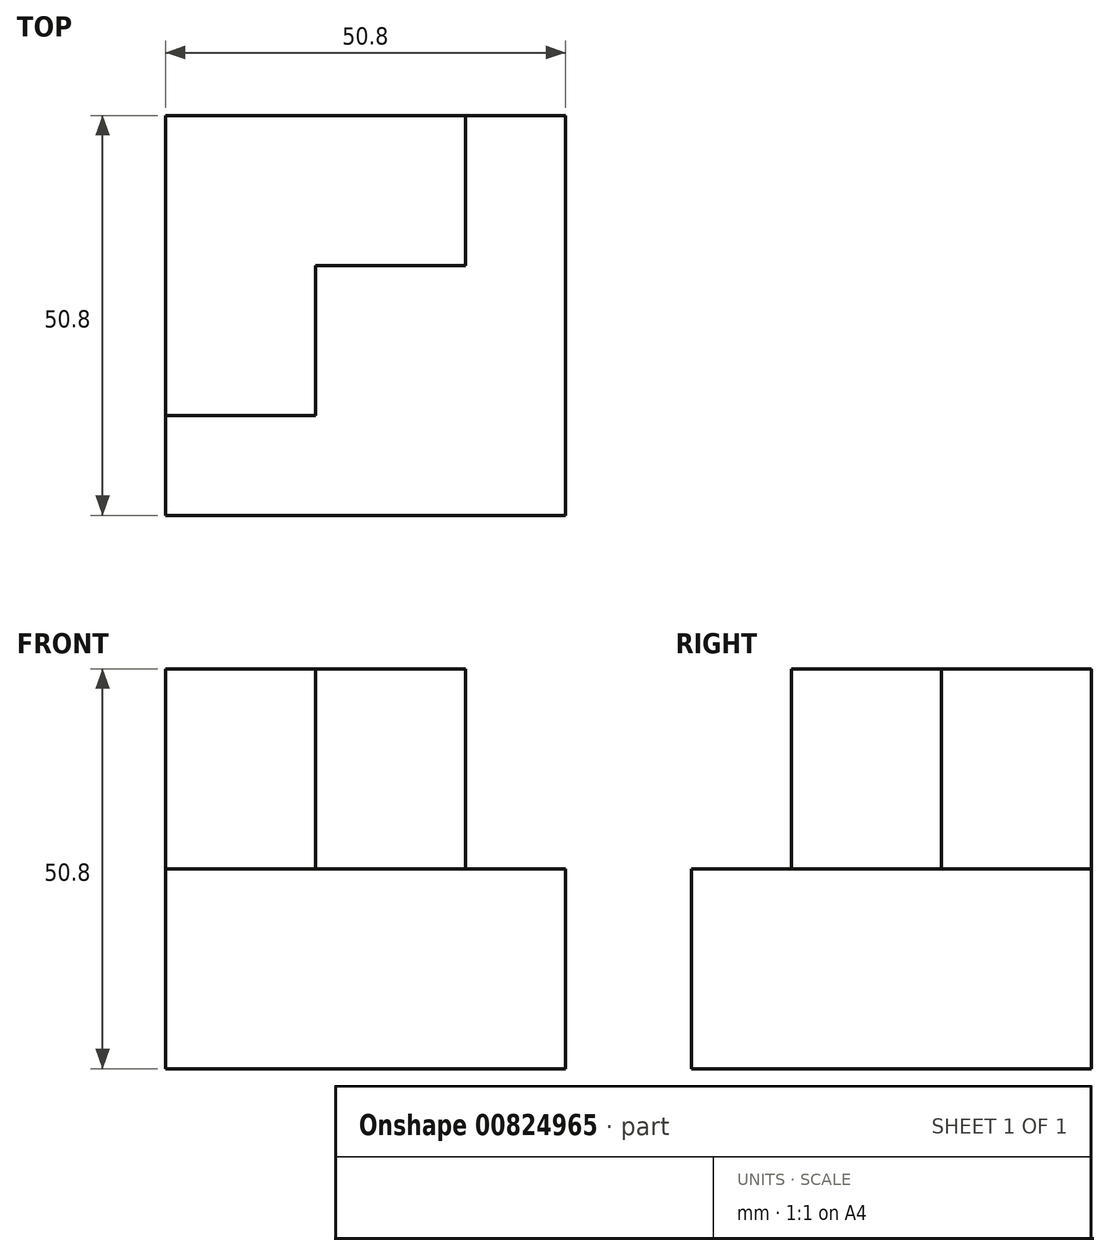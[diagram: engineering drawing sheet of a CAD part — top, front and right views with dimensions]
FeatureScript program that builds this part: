
annotation { "Feature Type Name" : "Feature", "Feature Type Description" : "" }
export const myFeature = defineFeature(function(context is Context, id is Id, definition is map)
    precondition{}
    {
        {
            var Q0;
            Q0=qCreatedBy(makeId("Top.planeOp"),FACE);
            var sketch = newSketch(context, id + "F0", { "sketchPlane" : qUnion([Q0])});
            skLineSegment(sketch, "E0.bottom", {"start": v(0, 0) * mm, "end": v(50.8, 0) * mm});
            skLineSegment(sketch, "E0.top", {"start": v(0, 50.8) * mm, "end": v(50.8, 50.8) * mm});
            skLineSegment(sketch, "E0.left", {"start": v(0, 0) * mm, "end": v(0, 50.8) * mm});
            skLineSegment(sketch, "E0.right", {"start": v(50.8, 0) * mm, "end": v(50.8, 50.8) * mm});
            skSolve(sketch);
        }
        {
            var Q0;
            Q0=makeQuery(id+"F0.imprint","IMPRINT",FACE,{"disambiguationData":[TD([[makeQuery(id+"F0.imprint","IMPRINT",EDGE,{"derivedFrom":sQuery(id+"F0.wireOp",EDGE,"E0.bottom")}),1.0]])]});
            extrude(context, id + "F1", {"entities" : qUnion([Q0]), "depth" : 25.4 * mm, "offsetDistance" : 25.4 * mm});
        }
        {
            var Q0;
            Q0=makeQuery(id+"F1.opExtrude","CAP_FACE",FACE,{"disambiguationData":[OSD([sQuery(id+"F0.wireOp",EDGE,"E0.bottom"),sQuery(id+"F0.wireOp",EDGE,"E0.top"),sQuery(id+"F0.wireOp",EDGE,"E0.left"),sQuery(id+"F0.wireOp",EDGE,"E0.right")])],"isStart":false});
            var sketch = newSketch(context, id + "F2", { "sketchPlane" : qUnion([Q0])});
            skLineSegment(sketch, "E1", {"start": v(0, 50.8) * mm, "end": v(38.1, 50.8) * mm});
            skLineSegment(sketch, "E2", {"start": v(38.1, 50.8) * mm, "end": v(38.1, 31.75) * mm});
            skLineSegment(sketch, "E3", {"start": v(38.1, 31.75) * mm, "end": v(19.05, 31.75) * mm});
            skLineSegment(sketch, "E4", {"start": v(19.05, 31.75) * mm, "end": v(19.05, 12.7) * mm});
            skLineSegment(sketch, "E5", {"start": v(19.05, 12.7) * mm, "end": v(0, 12.7) * mm});
            skLineSegment(sketch, "E6", {"start": v(0, 12.7) * mm, "end": v(0, 50.8) * mm});
            skSolve(sketch);
        }
        {
            var Q0;
            Q0=makeQuery(id+"F2.imprint","IMPRINT",FACE,{"disambiguationData":[TD([[makeQuery(id+"F2.imprint","IMPRINT",EDGE,{"derivedFrom":sQuery(id+"F2.wireOp",EDGE,"E1")}),-1.0]])]});
            extrude(context, id + "F3", {"entities" : qUnion([Q0]), "operationType" : NewBodyOperationType.ADD, "depth" : 25.4 * mm, "offsetDistance" : 25.4 * mm});
        }
    });
